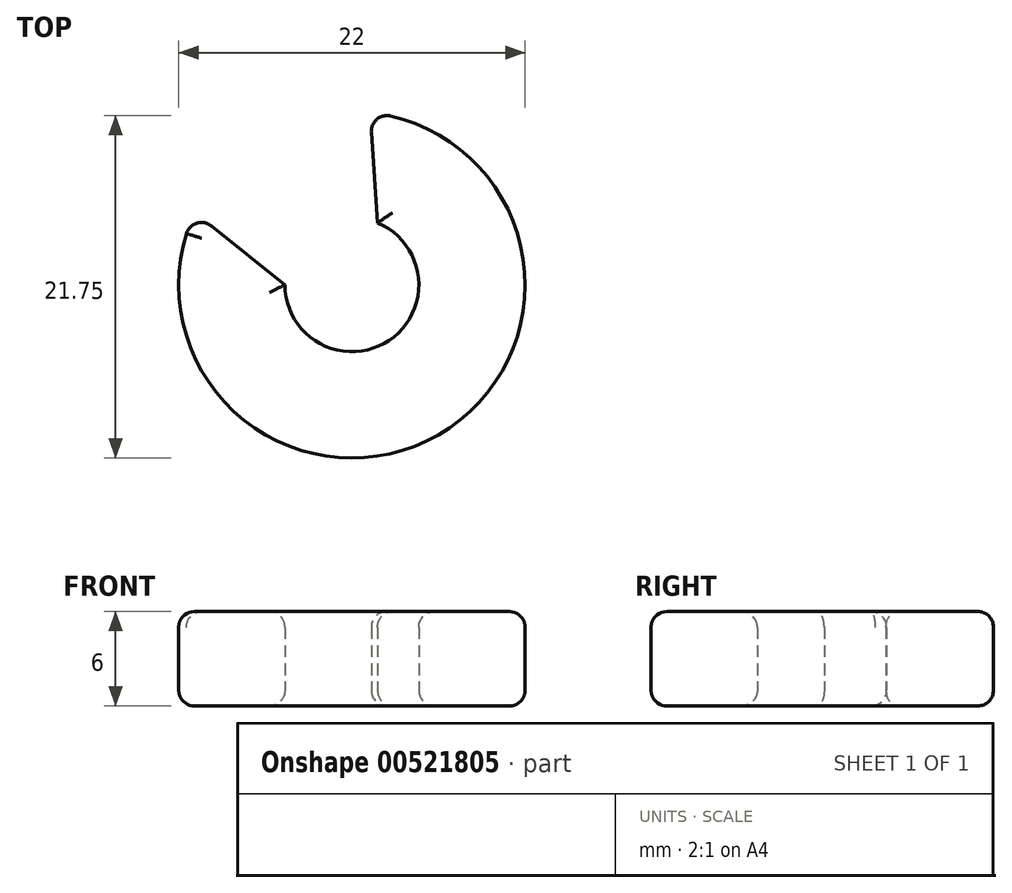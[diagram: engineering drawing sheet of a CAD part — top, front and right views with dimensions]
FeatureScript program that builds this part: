
annotation { "Feature Type Name" : "Feature", "Feature Type Description" : "" }
export const myFeature = defineFeature(function(context is Context, id is Id, definition is map)
    precondition{}
    {
        {
            var Q0;
            Q0=qCreatedBy(makeId("Top.planeOp"),FACE);
            var sketch = newSketch(context, id + "F0", { "sketchPlane" : qUnion([Q0])});
            skArc(sketch, "E0", {"start": v(-10, 4.6) * mm, "mid": v(5.44, -9.56) * mm, "end": v(1.15, 10.94) * mm});
            skArc(sketch, "E1", {"start": v(-4.25, 0) * mm, "mid": v(2.36, -3.53) * mm, "end": v(1.62, 3.93) * mm});
            skLineSegment(sketch, "E2", {"start": v(1.62, 3.93) * mm, "end": v(1.15, 10.94) * mm});
            skLineSegment(sketch, "E3", {"start": v(-4.25, 0) * mm, "end": v(-10, 4.6) * mm});
            skSolve(sketch);
        }
        {
            var Q0;
            Q0 = qSketchRegion(id + "F0", true);
            extrude(context, id + "F1", {"entities" : qUnion([Q0]), "depth" : 6 * mm, "offsetDistance" : 25 * mm});
        }
        {
            var Q0;
            Q0=makeQuery(id+"F1.opExtrude","CAP_EDGE",EDGE,{"disambiguationData":[OSD([sQuery(id+"F0.wireOp",EDGE,"E0")])],"isStart":false});
            var Q1;
            Q1=makeQuery(id+"F1.opExtrude","CAP_EDGE",EDGE,{"disambiguationData":[OSD([sQuery(id+"F0.wireOp",EDGE,"E1")])],"isStart":false});
            var Q2;
            Q2=makeQuery(id+"F1.opExtrude","CAP_EDGE",EDGE,{"disambiguationData":[OSD([sQuery(id+"F0.wireOp",EDGE,"E1")])],"isStart":true});
            var Q3;
            Q3=makeQuery(id+"F1.opExtrude","CAP_EDGE",EDGE,{"disambiguationData":[OSD([sQuery(id+"F0.wireOp",EDGE,"E0")])],"isStart":true});
            var Q4;
            Q4=makeQuery(id+"F1.opExtrude","CAP_EDGE",EDGE,{"disambiguationData":[OSD([sQuery(id+"F0.wireOp",EDGE,"E3")])],"isStart":true});
            var Q5;
            Q5=makeQuery(id+"F1.opExtrude","SWEPT_EDGE",EDGE,{"disambiguationData":[OSD([sQuery(id+"F0.wireOp",EDGE,"E0"),sQuery(id+"F0.wireOp",EDGE,"E3")])]});
            var Q6;
            Q6=makeQuery(id+"F1.opExtrude","CAP_EDGE",EDGE,{"disambiguationData":[OSD([sQuery(id+"F0.wireOp",EDGE,"E3")])],"isStart":false});
            var Q7;
            Q7=makeQuery(id+"F1.opExtrude","CAP_EDGE",EDGE,{"disambiguationData":[OSD([sQuery(id+"F0.wireOp",EDGE,"E2")])],"isStart":true});
            var Q8;
            Q8=makeQuery(id+"F1.opExtrude","SWEPT_EDGE",EDGE,{"disambiguationData":[OSD([sQuery(id+"F0.wireOp",EDGE,"E0"),sQuery(id+"F0.wireOp",EDGE,"E2")])]});
            var Q9;
            Q9=makeQuery(id+"F1.opExtrude","CAP_EDGE",EDGE,{"disambiguationData":[OSD([sQuery(id+"F0.wireOp",EDGE,"E2")])],"isStart":false});
            fillet(context, id + "F2", {"entities" : qUnion([Q0, Q1, Q2, Q3, Q4, Q5, Q6, Q7, Q8, Q9]), "radius" : 1 * mm, "tangentPropagation" : true, "allowEdgeOverflow" : false});
        }
    });
